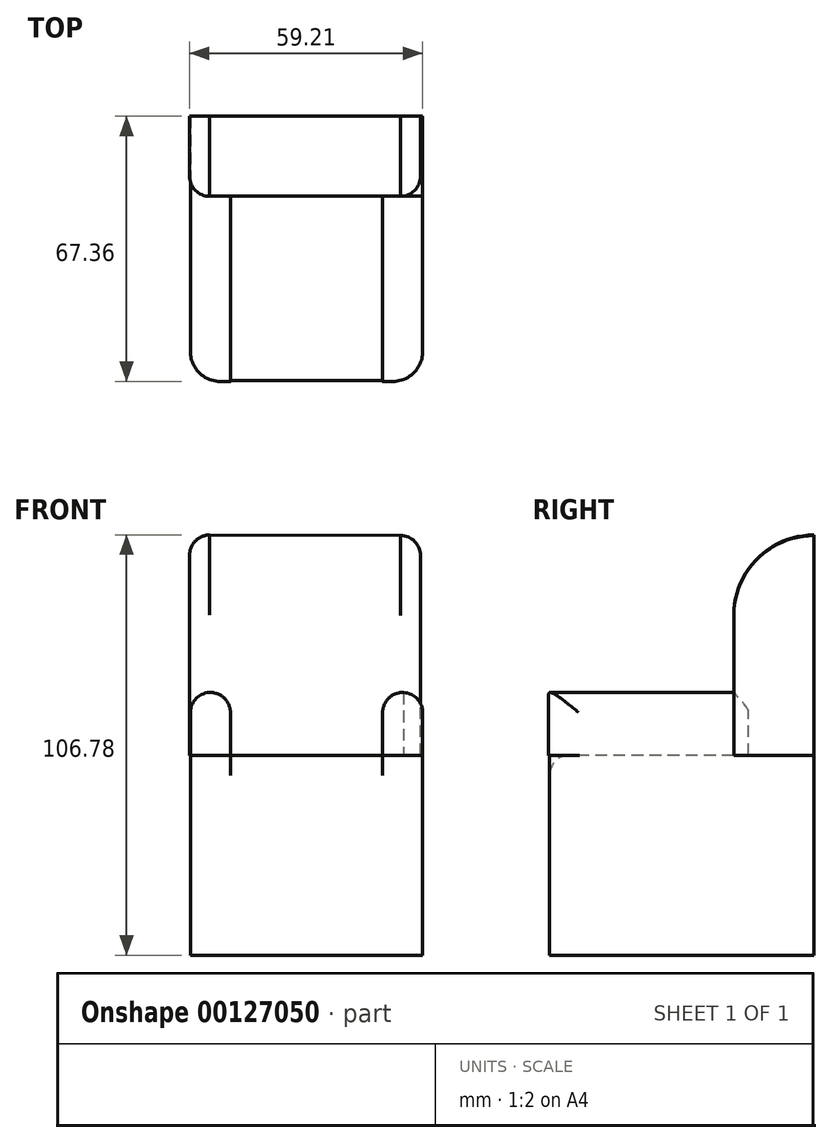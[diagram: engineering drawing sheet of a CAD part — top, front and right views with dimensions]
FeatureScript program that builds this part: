
annotation { "Feature Type Name" : "Feature", "Feature Type Description" : "" }
export const myFeature = defineFeature(function(context is Context, id is Id, definition is map)
    precondition{}
    {
        {
            var Q0;
            Q0=qCreatedBy(makeId("Front.planeOp"),FACE);
            var sketch = newSketch(context, id + "F0", { "sketchPlane" : qUnion([Q0])});
            skLineSegment(sketch, "E0", {"start": v(-29.33, 56) * mm, "end": v(-29.33, 0) * mm});
            skLineSegment(sketch, "E1", {"start": v(29.33, -0.18) * mm, "end": v(29.33, 55.81) * mm});
            skLineSegment(sketch, "E2", {"start": v(29.33, 55.81) * mm, "end": v(-29.33, 56) * mm});
            skLineSegment(sketch, "E3", {"start": v(-29.33, 0) * mm, "end": v(29.33, -0.18) * mm});
            skLineSegment(sketch, "E4", {"start": v(0, 55.9) * mm, "end": v(0, 0) * mm});
            skSolve(sketch);
        }
        {
            var Q0;
            Q0=qCreatedBy(makeId("Top.planeOp"),FACE);
            var sketch = newSketch(context, id + "F1", { "sketchPlane" : qUnion([Q0])});
            skLineSegment(sketch, "E5", {"start": v(-29.14, 0) * mm, "end": v(-29.14, -67.18) * mm});
            skLineSegment(sketch, "E6", {"start": v(29.88, -67.18) * mm, "end": v(29.88, 0) * mm});
            skLineSegment(sketch, "E7", {"start": v(29.88, 0) * mm, "end": v(-29.14, 0) * mm});
            skLineSegment(sketch, "E8", {"start": v(-29.14, -67.18) * mm, "end": v(29.88, -67.18) * mm});
            skSolve(sketch);
        }
        {
            var Q0;
            {var subQ1=sQuery(id+"F0.wireOp",EDGE,"E0");Q0=makeQuery(id+"F0.imprint","IMPRINT",FACE,{"disambiguationData":[TD([[makeQuery(id+"F0.imprint","IMPRINT",EDGE,{"derivedFrom":subQ1}),1.0]])]});}
            extrude(context, id + "F2", {"entities" : qUnion([Q0]), "depth" : 20.32 * mm});
        }
        {
            var Q0;
            Q0=makeQuery(id+"F1.imprint","IMPRINT",FACE,{"disambiguationData":[TD([[makeQuery(id+"F1.imprint","IMPRINT",EDGE,{"derivedFrom":sQuery(id+"F1.wireOp",EDGE,"E5")}),1.0]])]});
            extrude(context, id + "F3", {"entities" : qUnion([Q0]), "operationType" : NewBodyOperationType.ADD, "oppositeDirection" : true, "depth" : 50.8 * mm});
        }
        {
            var Q0;
            Q0=makeQuery(id+"F2.opExtrude","CAP_EDGE",EDGE,{"disambiguationData":[OSD([sQuery(id+"F0.wireOp",EDGE,"E2")])],"isStart":false});
            fillet(context, id + "F4", {"entities" : qUnion([Q0]), "radius" : 20.32 * mm, "tangentPropagation" : true, "allowEdgeOverflow" : false});
        }
        {
            var Q0;
            Q0=qCreatedBy(makeId("Top.planeOp"),FACE);
            var sketch = newSketch(context, id + "F5", { "sketchPlane" : qUnion([Q0])});
            skLineSegment(sketch, "E9", {"start": v(-29.14, -20.25) * mm, "end": v(-29.14, -67.36) * mm});
            skLineSegment(sketch, "E10", {"start": v(-29.14, -67.36) * mm, "end": v(-18.88, -67.36) * mm});
            skLineSegment(sketch, "E11", {"start": v(-29.14, -20.25) * mm, "end": v(-18.88, -20.25) * mm});
            skLineSegment(sketch, "E12", {"start": v(-18.88, -20.25) * mm, "end": v(-18.88, -67.36) * mm});
            skLineSegment(sketch, "E13", {"start": v(-18.88, -20.25) * mm, "end": v(29.88, -20.25) * mm, "construction": true});
            skLineSegment(sketch, "E14", {"start": v(29.88, -20.25) * mm, "end": v(29.88, -67.36) * mm});
            skLineSegment(sketch, "E15", {"start": v(29.88, -67.36) * mm, "end": v(-18.88, -67.36) * mm, "construction": true});
            skLineSegment(sketch, "E16", {"start": v(29.88, -67.36) * mm, "end": v(19.62, -67.36) * mm});
            skLineSegment(sketch, "E17", {"start": v(19.62, -67.36) * mm, "end": v(19.62, -20.25) * mm});
            skLineSegment(sketch, "E18", {"start": v(19.62, -20.25) * mm, "end": v(29.88, -20.25) * mm});
            skSolve(sketch);
        }
        {
            var Q0;
            Q0=makeQuery(id+"F5.imprint","IMPRINT",FACE,{"disambiguationData":[TD([[makeQuery(id+"F5.imprint","IMPRINT",EDGE,{"derivedFrom":sQuery(id+"F5.wireOp",EDGE,"E9")}),1.0]])]});
            var Q1;
            Q1=makeQuery(id+"F5.imprint","IMPRINT",FACE,{"disambiguationData":[TD([[makeQuery(id+"F5.imprint","IMPRINT",EDGE,{"derivedFrom":sQuery(id+"F5.wireOp",EDGE,"E14")}),-1.0]])]});
            extrude(context, id + "F6", {"entities" : qUnion([Q0, Q1]), "operationType" : NewBodyOperationType.ADD, "depth" : 17.78 * mm});
        }
        {
            var Q0;
            Q0=makeQuery(id+"F6.opExtrude","CAP_EDGE",EDGE,{"disambiguationData":[OSD([sQuery(id+"F5.wireOp",EDGE,"E17")])],"isStart":false});
            var Q1;
            Q1=makeQuery(id+"F6.opExtrude","CAP_EDGE",EDGE,{"disambiguationData":[OSD([sQuery(id+"F5.wireOp",EDGE,"E12")])],"isStart":false});
            fillet(context, id + "F7", {"entities" : qUnion([Q0, Q1]), "radius" : 7.62 * mm, "tangentPropagation" : true, "allowEdgeOverflow" : false});
        }
        {
            var Q0;
            Q0=makeQuery(id+"F3.opExtrude","SWEPT_EDGE",EDGE,{"disambiguationData":[OSD([sQuery(id+"F1.wireOp",EDGE,"E5"),sQuery(id+"F1.wireOp",EDGE,"E8")])]});
            var Q1;
            Q1=makeQuery(id+"F3.opExtrude","SWEPT_EDGE",EDGE,{"disambiguationData":[OSD([sQuery(id+"F1.wireOp",EDGE,"E6"),sQuery(id+"F1.wireOp",EDGE,"E8")])]});
            fillet(context, id + "F8", {"entities" : qUnion([Q0, Q1]), "radius" : 7.62 * mm, "tangentPropagation" : true, "allowEdgeOverflow" : false});
        }
        {
            var Q0;
            Q0=makeQuery(id+"F6.opExtrude","SWEPT_EDGE",EDGE,{"disambiguationData":[OSD([sQuery(id+"F5.wireOp",EDGE,"E14"),sQuery(id+"F5.wireOp",EDGE,"E16")])]});
            var Q1;
            Q1=makeQuery(id+"F6.opExtrude","SWEPT_EDGE",EDGE,{"disambiguationData":[OSD([sQuery(id+"F5.wireOp",EDGE,"E9"),sQuery(id+"F5.wireOp",EDGE,"E10")])]});
            fillet(context, id + "F9", {"entities" : qUnion([Q0, Q1]), "radius" : 7.62 * mm, "tangentPropagation" : true, "allowEdgeOverflow" : false});
        }
        {
            var Q0;
            Q0=makeQuery(id+"F2.opExtrude","CAP_EDGE",EDGE,{"disambiguationData":[OSD([sQuery(id+"F0.wireOp",EDGE,"E0")])],"isStart":false});
            var Q1;
            Q1=makeQuery(id+"F2.opExtrude","CAP_EDGE",EDGE,{"disambiguationData":[OSD([sQuery(id+"F0.wireOp",EDGE,"E1")])],"isStart":false});
            var Q2;
            {var subQ0=sQuery(id+"F5.wireOp",EDGE,"E12");var subQ1=sQuery(id+"F1.wireOp",EDGE,"E8");var subQ2=sQuery(id+"F5.wireOp",EDGE,"E17");Q2=makeQuery(id+"F6.boolean.opBoolean","SPLIT",EDGE,{"disambiguationData":[TD([makeQuery(id+"F3.opExtrude","CAP_FACE",FACE,{"disambiguationData":[OSD([sQuery(id+"F1.wireOp",EDGE,"E5"),sQuery(id+"F1.wireOp",EDGE,"E6"),sQuery(id+"F1.wireOp",EDGE,"E7"),subQ1])],"isStart":true}),makeQuery(id+"F3.opExtrude","SWEPT_FACE",FACE,{"disambiguationData":[OSD([subQ1])]}),makeQuery(id+"F6.opExtrude","CAP_FACE",FACE,{"disambiguationData":[OSD([sQuery(id+"F5.wireOp",EDGE,"E9"),sQuery(id+"F5.wireOp",EDGE,"E10"),sQuery(id+"F5.wireOp",EDGE,"E11"),subQ0])],"isStart":true}),makeQuery(id+"F6.opExtrude","SWEPT_FACE",FACE,{"disambiguationData":[OSD([subQ0])]}),makeQuery(id+"F6.opExtrude","CAP_FACE",FACE,{"disambiguationData":[OSD([sQuery(id+"F5.wireOp",EDGE,"E14"),sQuery(id+"F5.wireOp",EDGE,"E16"),subQ2,sQuery(id+"F5.wireOp",EDGE,"E18")])],"isStart":true}),makeQuery(id+"F6.opExtrude","SWEPT_FACE",FACE,{"disambiguationData":[OSD([subQ2])]})])],"derivedFrom":makeQuery(id+"F3.opExtrude","CAP_EDGE",EDGE,{"disambiguationData":[OSD([subQ1])],"isStart":true})});}
            fillet(context, id + "F10", {"entities" : qUnion([Q0, Q1, Q2]), "radius" : 5.08 * mm, "tangentPropagation" : true, "allowEdgeOverflow" : false});
        }
        {
            var Q0;
            Q0=makeQuery(id+"F6.opExtrude","CAP_EDGE",EDGE,{"disambiguationData":[OSD([sQuery(id+"F5.wireOp",EDGE,"E9")])],"isStart":false});
            var Q1;
            Q1=makeQuery(id+"F6.opExtrude","CAP_EDGE",EDGE,{"disambiguationData":[OSD([sQuery(id+"F5.wireOp",EDGE,"E14")])],"isStart":false});
            fillet(context, id + "F11", {"entities" : qUnion([Q0, Q1]), "radius" : 5.08 * mm, "allowEdgeOverflow" : false});
        }
    });
